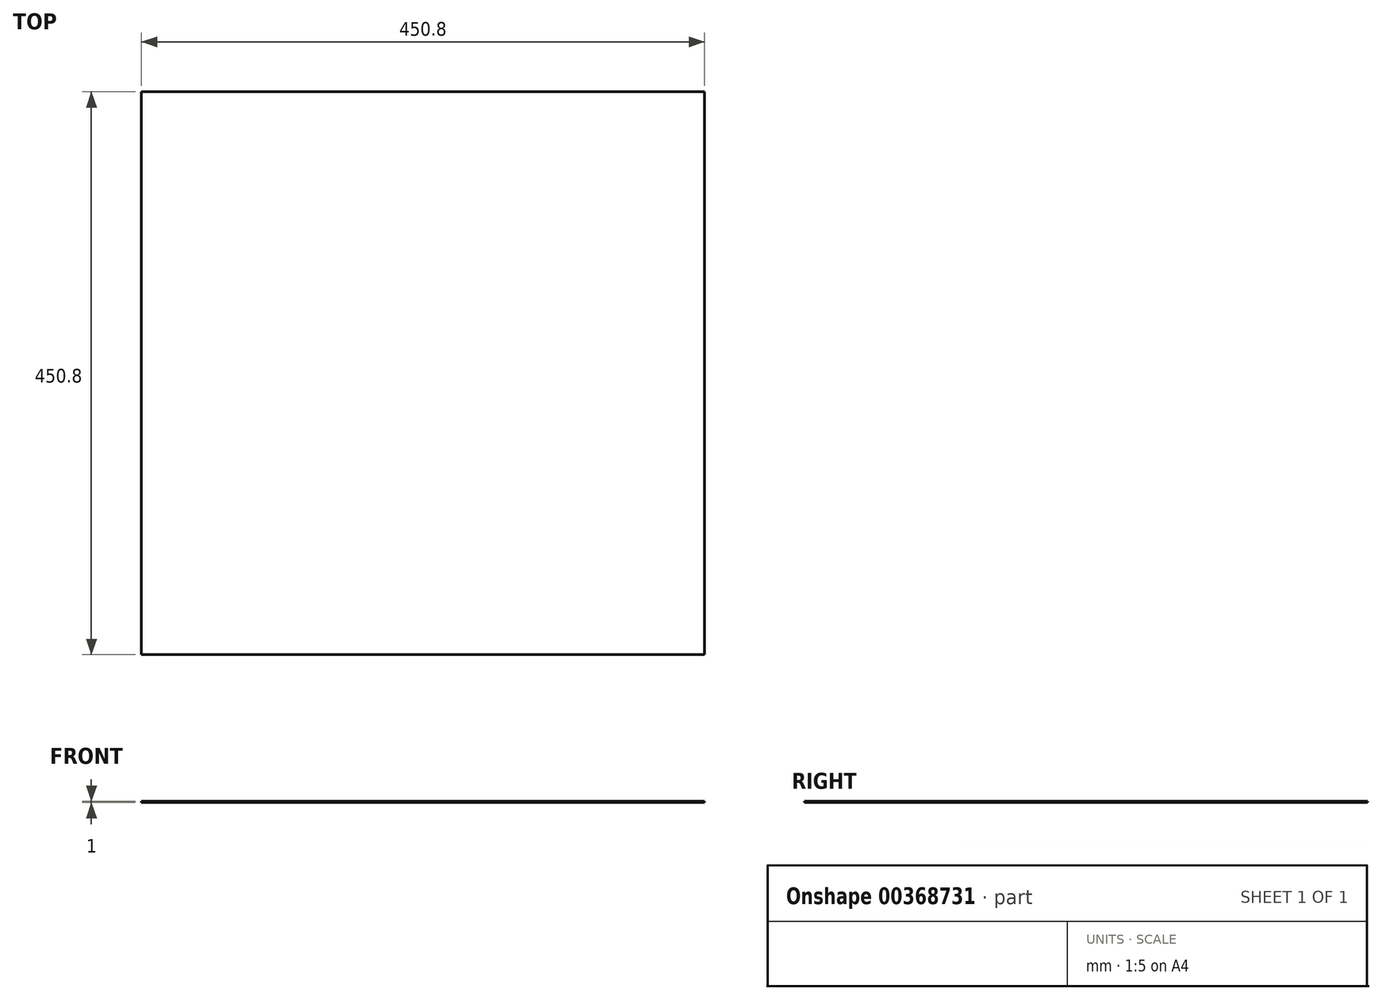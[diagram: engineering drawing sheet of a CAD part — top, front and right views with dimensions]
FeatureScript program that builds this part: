
annotation { "Feature Type Name" : "Feature", "Feature Type Description" : "" }
export const myFeature = defineFeature(function(context is Context, id is Id, definition is map)
    precondition{}
    {
        {
            var Q0;
            Q0=qCreatedBy(makeId("Top.planeOp"),FACE);
            var sketch = newSketch(context, id + "F0", { "sketchPlane" : qUnion([Q0])});
            skLineSegment(sketch, "E0.bottom", {"start": v(225.4, 225.4) * mm, "end": v(-225.4, 225.4) * mm});
            skLineSegment(sketch, "E0.top", {"start": v(225.4, -225.4) * mm, "end": v(-225.4, -225.4) * mm});
            skLineSegment(sketch, "E0.left", {"start": v(225.4, 225.4) * mm, "end": v(225.4, -225.4) * mm});
            skLineSegment(sketch, "E0.right", {"start": v(-225.4, 225.4) * mm, "end": v(-225.4, -225.4) * mm});
            skPoint(sketch, "E0.middle", {"position": v(0, 0) * mm});
            skSolve(sketch);
        }
        {
            var Q0;
            Q0=makeQuery(id+"F0.imprint","IMPRINT",FACE,{"disambiguationData":[TD([[makeQuery(id+"F0.imprint","IMPRINT",EDGE,{"derivedFrom":sQuery(id+"F0.wireOp",EDGE,"E0.bottom")}),1.0]])]});
            extrude(context, id + "F1", {"entities" : qUnion([Q0]), "depth" : 1 * mm});
        }
    });
